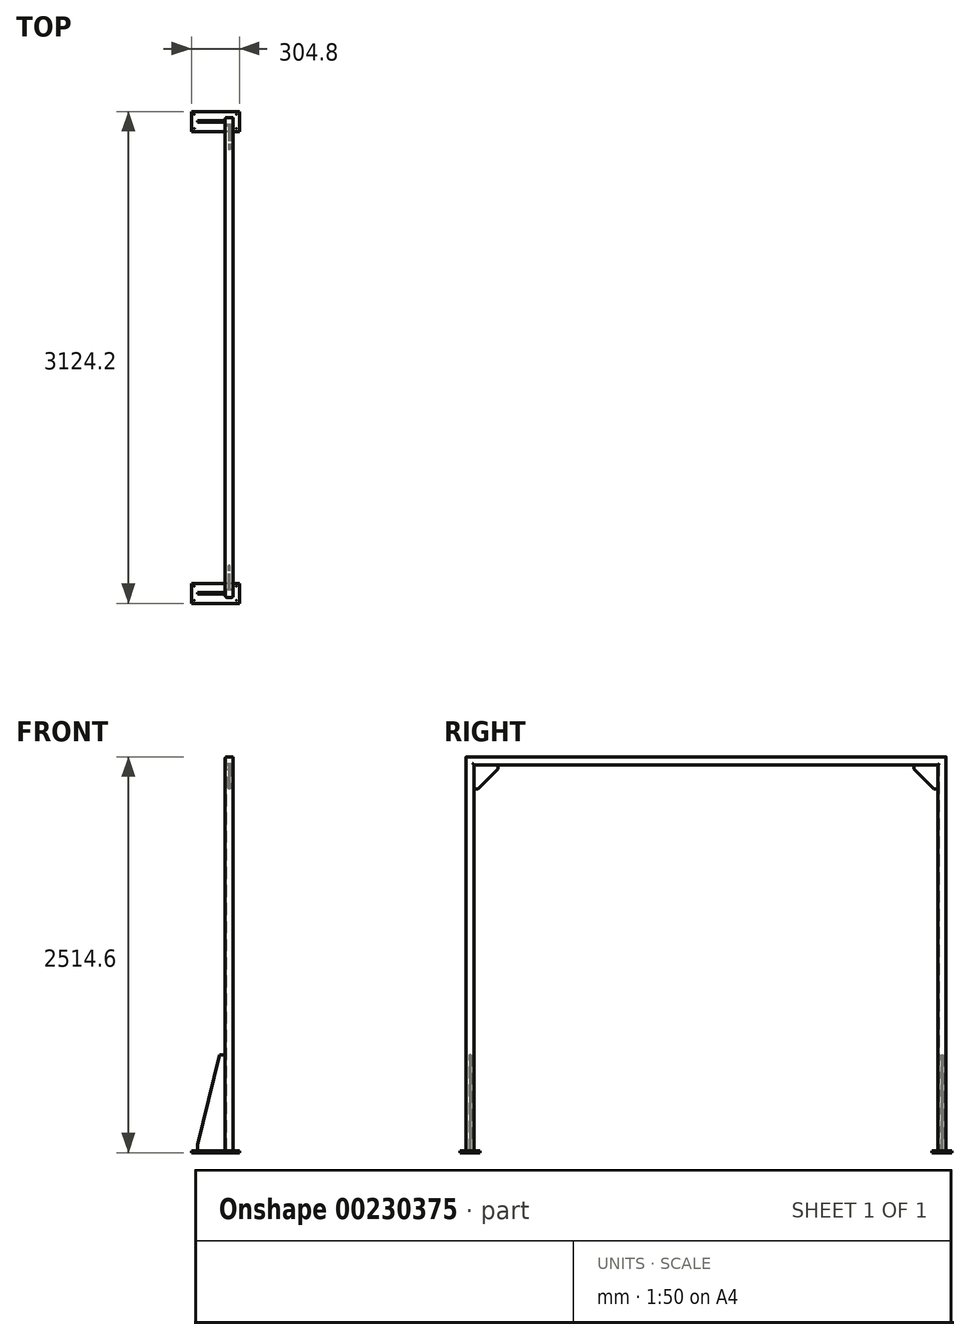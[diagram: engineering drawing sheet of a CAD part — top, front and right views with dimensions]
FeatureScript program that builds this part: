
annotation { "Feature Type Name" : "Feature", "Feature Type Description" : "" }
export const myFeature = defineFeature(function(context is Context, id is Id, definition is map)
    precondition{}
    {
        {
            var Q0;
            Q0=qCreatedBy(makeId("Right.planeOp"),FACE);
            var sketch = newSketch(context, id + "F0", { "sketchPlane" : qUnion([Q0])});
            skLineSegment(sketch, "E0.top", {"start": v(-1524, 2501.9) * mm, "end": v(1524, 2501.9) * mm});
            skLineSegment(sketch, "E0.left", {"start": v(-1524, 0) * mm, "end": v(-1524, 2501.9) * mm});
            skLineSegment(sketch, "E0.right", {"start": v(1524, 0) * mm, "end": v(1524, 2501.9) * mm});
            skSolve(sketch);
        }
        {
            var Q0;
            Q0=qCreatedBy(makeId("Top.planeOp"),FACE);
            var sketch = newSketch(context, id + "F1", { "sketchPlane" : qUnion([Q0])});
            skPoint(sketch, "E1.0", {"position": v(0, -1524) * mm});
            skLineSegment(sketch, "E2", {"start": v(0, -1524) * mm, "end": v(15.75, -1524) * mm});
            skLineSegment(sketch, "E3", {"start": v(25.4, -1514.35) * mm, "end": v(25.4, -1482.85) * mm});
            skLineSegment(sketch, "E4", {"start": v(15.75, -1473.2) * mm, "end": v(-15.75, -1473.2) * mm});
            skLineSegment(sketch, "E5", {"start": v(-25.4, -1482.85) * mm, "end": v(-25.4, -1514.35) * mm});
            skLineSegment(sketch, "E6", {"start": v(-15.75, -1524) * mm, "end": v(0, -1524) * mm});
            skPoint(sketch, "E7.visualSharp", {"position": v(25.4, -1524) * mm});
            skArc(sketch, "E7.filletArc", {"start": v(15.75, -1524) * mm, "mid": v(22.57, -1521.17) * mm, "end": v(25.4, -1514.35) * mm});
            skPoint(sketch, "E8.visualSharp", {"position": v(25.4, -1473.2) * mm});
            skArc(sketch, "E8.filletArc", {"start": v(25.4, -1482.85) * mm, "mid": v(22.57, -1476.03) * mm, "end": v(15.75, -1473.2) * mm});
            skPoint(sketch, "E9.visualSharp", {"position": v(-25.4, -1473.2) * mm});
            skArc(sketch, "E9.filletArc", {"start": v(-15.75, -1473.2) * mm, "mid": v(-22.57, -1476.03) * mm, "end": v(-25.4, -1482.85) * mm});
            skPoint(sketch, "E10.visualSharp", {"position": v(-25.4, -1524) * mm});
            skArc(sketch, "E10.filletArc", {"start": v(-25.4, -1514.35) * mm, "mid": v(-22.57, -1521.17) * mm, "end": v(-15.75, -1524) * mm});
            skLineSegment(sketch, "E11.0", {"start": v(-15.75, -1519.24) * mm, "end": v(0, -1519.24) * mm});
            skArc(sketch, "E11.1", {"start": v(-20.64, -1514.35) * mm, "mid": v(-19.2, -1517.8) * mm, "end": v(-15.75, -1519.24) * mm});
            skLineSegment(sketch, "E11.2", {"start": v(-20.64, -1482.85) * mm, "end": v(-20.64, -1514.35) * mm});
            skArc(sketch, "E11.3", {"start": v(-15.75, -1477.96) * mm, "mid": v(-19.2, -1479.4) * mm, "end": v(-20.64, -1482.85) * mm});
            skArc(sketch, "E11.4", {"start": v(15.75, -1519.24) * mm, "mid": v(19.2, -1517.8) * mm, "end": v(20.64, -1514.35) * mm});
            skLineSegment(sketch, "E11.5", {"start": v(20.64, -1514.35) * mm, "end": v(20.64, -1482.85) * mm});
            skArc(sketch, "E11.6", {"start": v(20.64, -1482.85) * mm, "mid": v(19.2, -1479.4) * mm, "end": v(15.75, -1477.96) * mm});
            skLineSegment(sketch, "E11.7", {"start": v(15.75, -1477.96) * mm, "end": v(-15.75, -1477.96) * mm});
            skLineSegment(sketch, "E12.0", {"start": v(0, -1519.24) * mm, "end": v(15.75, -1519.24) * mm});
            skSolve(sketch);
        }
        {
            var Q0;
            Q0=makeQuery(id+"F1.imprint","IMPRINT",FACE,{"disambiguationData":[TD([[makeQuery(id+"F1.imprint","IMPRINT",EDGE,{"derivedFrom":sQuery(id+"F1.wireOp",EDGE,"E2")}),1.0]])]});
            var Q1;
            Q1=sQuery(id+"F0.wireOp",EDGE,"E0.left");
            var Q2;
            Q2=sQuery(id+"F0.wireOp",EDGE,"E0.top");
            var Q3;
            Q3=sQuery(id+"F0.wireOp",EDGE,"E0.right");
            sweep(context, id + "F2", {"profiles" : qUnion([Q0]), "path" : qUnion([Q1, Q2, Q3])});
        }
        {
            var Q0;
            Q0=makeQuery(id+"F2.opSweep","CAP_FACE",FACE,{"disambiguationData":[OSD([sQuery(id+"F0.wireOp",VERTEX,"E0.left.start"),sQuery(id+"F1.wireOp",EDGE,"E2"),sQuery(id+"F1.wireOp",EDGE,"E3"),sQuery(id+"F1.wireOp",EDGE,"E4"),sQuery(id+"F1.wireOp",EDGE,"E5"),sQuery(id+"F1.wireOp",EDGE,"E6"),sQuery(id+"F1.wireOp",EDGE,"E7.filletArc"),sQuery(id+"F1.wireOp",EDGE,"E8.filletArc"),sQuery(id+"F1.wireOp",EDGE,"E9.filletArc"),sQuery(id+"F1.wireOp",EDGE,"E10.filletArc"),sQuery(id+"F1.wireOp",EDGE,"E11.0"),sQuery(id+"F1.wireOp",EDGE,"E11.1"),sQuery(id+"F1.wireOp",EDGE,"E11.2"),sQuery(id+"F1.wireOp",EDGE,"E11.3"),sQuery(id+"F1.wireOp",EDGE,"E11.4"),sQuery(id+"F1.wireOp",EDGE,"E11.5"),sQuery(id+"F1.wireOp",EDGE,"E11.6"),sQuery(id+"F1.wireOp",EDGE,"E11.7"),sQuery(id+"F1.wireOp",EDGE,"E12.0")])],"isStart":true});
            var sketch = newSketch(context, id + "F3", { "sketchPlane" : qUnion([Q0])});
            skLineSegment(sketch, "E13.0", {"start": v(-15.75, 1524) * mm, "end": v(15.75, 1524) * mm, "construction": true});
            skLineSegment(sketch, "E14.0", {"start": v(15.75, 1473.2) * mm, "end": v(-15.75, 1473.2) * mm, "construction": true});
            skLineSegment(sketch, "E15", {"start": v(0, 1524) * mm, "end": v(0, 1473.2) * mm, "construction": true});
            skLineSegment(sketch, "E16.bottom", {"start": v(63.5, 1562.1) * mm, "end": v(-63.5, 1562.1) * mm});
            skLineSegment(sketch, "E16.top", {"start": v(63.5, 1435.1) * mm, "end": v(-63.5, 1435.1) * mm});
            skLineSegment(sketch, "E16.left", {"start": v(63.5, 1562.1) * mm, "end": v(63.5, 1435.1) * mm});
            skLineSegment(sketch, "E16.right", {"start": v(-63.5, 1562.1) * mm, "end": v(-63.5, 1435.1) * mm});
            skPoint(sketch, "E16.middle", {"position": v(0, 1498.6) * mm});
            skLineSegment(sketch, "E17.bottom", {"start": v(-63.5, 1435.1) * mm, "end": v(-241.3, 1435.1) * mm});
            skLineSegment(sketch, "E17.top", {"start": v(-63.5, 1562.1) * mm, "end": v(-241.3, 1562.1) * mm});
            skLineSegment(sketch, "E17.left", {"start": v(-63.5, 1435.1) * mm, "end": v(-63.5, 1562.1) * mm});
            skLineSegment(sketch, "E17.right", {"start": v(-241.3, 1435.1) * mm, "end": v(-241.3, 1562.1) * mm});
            skLineSegment(sketch, "E18.0", {"start": v(-15.75, -1473.2) * mm, "end": v(15.75, -1473.2) * mm, "construction": true});
            skLineSegment(sketch, "E19.0", {"start": v(-15.75, -1524) * mm, "end": v(15.75, -1524) * mm, "construction": true});
            skLineSegment(sketch, "E20", {"start": v(0, -1473.2) * mm, "end": v(0, -1524) * mm, "construction": true});
            skLineSegment(sketch, "E21", {"start": v(0, -1501.83) * mm, "end": v(-72.48, -1501.83) * mm, "construction": true});
            skSolve(sketch);
        }
        {
            var Q0;
            Q0 = qSketchRegion(id + "F3", true);
            extrude(context, id + "F4", {"entities" : qUnion([Q0]), "depth" : 12.7 * mm});
        }
        {
            var Q0;
            Q0=makeQuery(id+"F4.opExtrude","SWEPT_FACE",FACE,{"disambiguationData":[OSD([sQuery(id+"F3.wireOp",EDGE,"E16.top"),sQuery(id+"F3.wireOp",EDGE,"E17.bottom")])]});
            var Q1;
            Q1=makeQuery(id+"F4.opExtrude","SWEPT_FACE",FACE,{"disambiguationData":[OSD([sQuery(id+"F3.wireOp",EDGE,"E16.bottom"),sQuery(id+"F3.wireOp",EDGE,"E17.top")])]});
            cPlane(context, id + "F5", {"entities" : qUnion([Q0, Q1]), "cplaneType" : CPlaneType.MID_PLANE, "offset" : 25.4 * mm, "width" : 152.4 * mm, "height" : 152.4 * mm});
        }
        {
            var Q0;
            Q0=qCreatedBy(id+"F5.planeOp",FACE);
            var sketch = newSketch(context, id + "F6", { "sketchPlane" : qUnion([Q0])});
            skLineSegment(sketch, "E22.0", {"start": v(25.4, 2492.25) * mm, "end": v(25.4, 0) * mm, "construction": true});
            skLineSegment(sketch, "E23.bottom", {"start": v(25.4, 0) * mm, "end": v(203.2, 0) * mm});
            skLineSegment(sketch, "E23.top", {"start": v(25.4, 609.6) * mm, "end": v(63.5, 609.6) * mm});
            skLineSegment(sketch, "E23.left", {"start": v(25.4, 0) * mm, "end": v(25.4, 609.6) * mm});
            skLineSegment(sketch, "E23.right", {"start": v(203.2, 0) * mm, "end": v(203.2, 38.1) * mm});
            skLineSegment(sketch, "E24.0", {"start": v(25.4, 38.1) * mm, "end": v(203.2, 38.1) * mm});
            skLineSegment(sketch, "E25.0", {"start": v(63.5, 2492.25) * mm, "end": v(63.5, 0) * mm});
            skLineSegment(sketch, "E26", {"start": v(63.5, 609.6) * mm, "end": v(203.2, 38.1) * mm});
            skSolve(sketch);
        }
        {
            var Q0;
            Q0 = qSketchRegion(id + "F6", true);
            extrude(context, id + "F7", {"entities" : qUnion([Q0]), "endBound" : BoundingType.SYMMETRIC, "depth" : 9.65 * mm});
        }
        {
            var Q0;
            Q0=makeQuery(id+"F4.opExtrude","CAP_FACE",FACE,{"disambiguationData":[OSD([sQuery(id+"F3.wireOp",EDGE,"E16.bottom"),sQuery(id+"F3.wireOp",EDGE,"E16.top"),sQuery(id+"F3.wireOp",EDGE,"E16.left"),sQuery(id+"F3.wireOp",EDGE,"E17.bottom"),sQuery(id+"F3.wireOp",EDGE,"E17.top"),sQuery(id+"F3.wireOp",EDGE,"E17.right")])],"isStart":false});
            var sketch = newSketch(context, id + "F8", { "sketchPlane" : qUnion([Q0])});
            skLineSegment(sketch, "E27.0", {"start": v(-222.25, 1435.1) * mm, "end": v(-222.25, 1562.1) * mm, "construction": true});
            skLineSegment(sketch, "E28.0", {"start": v(63.5, 1543.05) * mm, "end": v(-266.7, 1543.05) * mm, "construction": true});
            skLineSegment(sketch, "E29.0", {"start": v(44.45, 1562.1) * mm, "end": v(44.45, 1435.1) * mm, "construction": true});
            skLineSegment(sketch, "E30.0", {"start": v(63.5, 1454.15) * mm, "end": v(-266.7, 1454.15) * mm, "construction": true});
            skPoint(sketch, "E31", {"position": v(-222.25, 1454.15) * mm});
            skPoint(sketch, "E32", {"position": v(-222.25, 1543.05) * mm});
            skPoint(sketch, "E33", {"position": v(44.45, 1543.05) * mm});
            skPoint(sketch, "E34", {"position": v(44.45, 1454.15) * mm});
            skSolve(sketch);
        }
        {
            var Q0;
            Q0=sQuery(id+"F8.wireOp",VERTEX,"E31");
            var Q1;
            Q1=sQuery(id+"F8.wireOp",VERTEX,"E32");
            var Q2;
            Q2=sQuery(id+"F8.wireOp",VERTEX,"E33");
            var Q3;
            Q3=sQuery(id+"F8.wireOp",VERTEX,"E34");
            var Q4;
            Q4=makeQuery(id+"F4.opExtrude","SWEPT_BODY",BODY,{"disambiguationData":[OSD([sQuery(id+"F3.wireOp",EDGE,"E16.bottom"),sQuery(id+"F3.wireOp",EDGE,"E16.top"),sQuery(id+"F3.wireOp",EDGE,"E16.left"),sQuery(id+"F3.wireOp",EDGE,"E17.bottom"),sQuery(id+"F3.wireOp",EDGE,"E17.top"),sQuery(id+"F3.wireOp",EDGE,"E17.right")])]});
            hole(context, id + "F9", {"style" : HoleStyle.SIMPLE, "endStyle" : HoleEndStyle.THROUGH, "standardTappedOrClearance" : lookupTablePath({ "standard" : "ANSI", "size" : "9/16 (0.56)", "type" : "Drilled" }), "standardBlindInLast" : lookupTablePath({ "standard" : "ANSI", "size" : "9/16", "type" : "Drilled" }), "holeDiameter" : 9 / 406.4 * mm, "startFromSketch" : true, "locations" : qUnion([Q0, Q1, Q2, Q3]), "scope" : qUnion([Q4]), "isTappedThrough" : true});
        }
        {
            var Q0;
            Q0=makeQuery(id+"F4.opExtrude","SWEPT_BODY",BODY,{"disambiguationData":[OSD([sQuery(id+"F3.wireOp",EDGE,"E16.bottom"),sQuery(id+"F3.wireOp",EDGE,"E16.top"),sQuery(id+"F3.wireOp",EDGE,"E16.left"),sQuery(id+"F3.wireOp",EDGE,"E17.bottom"),sQuery(id+"F3.wireOp",EDGE,"E17.top"),sQuery(id+"F3.wireOp",EDGE,"E17.right")])]});
            var Q1;
            Q1=makeQuery(id+"F7.opExtrude","SWEPT_BODY",BODY,{"disambiguationData":[OSD([sQuery(id+"F6.wireOp",EDGE,"E23.bottom"),sQuery(id+"F6.wireOp",EDGE,"E23.top"),sQuery(id+"F6.wireOp",EDGE,"E23.left"),sQuery(id+"F6.wireOp",EDGE,"E23.right"),sQuery(id+"F6.wireOp",EDGE,"E26")])]});
            var Q2;
            Q2=qCreatedBy(makeId("Front.planeOp"),FACE);
            mirror(context, id + "F10", {"entities" : qUnion([Q0, Q1]), "mirrorPlane" : qUnion([Q2])});
        }
        {
            var Q0;
            Q0=makeQuery(id+"F2.opSweep","SWEPT_FACE",FACE,{"disambiguationData":[OSD([sQuery(id+"F0.wireOp",EDGE,"E0.left"),sQuery(id+"F1.wireOp",EDGE,"E3")])]});
            var Q1;
            Q1=makeQuery(id+"F2.opSweep","SWEPT_FACE",FACE,{"disambiguationData":[OSD([sQuery(id+"F0.wireOp",EDGE,"E0.left"),sQuery(id+"F1.wireOp",EDGE,"E5")])]});
            cPlane(context, id + "F11", {"entities" : qUnion([Q0, Q1]), "cplaneType" : CPlaneType.MID_PLANE, "offset" : 25.4 * mm, "width" : 152.4 * mm, "height" : 152.4 * mm});
        }
        {
            var Q0;
            Q0=qCreatedBy(id+"F11.planeOp",FACE);
            var sketch = newSketch(context, id + "F12", { "sketchPlane" : qUnion([Q0])});
            skLineSegment(sketch, "E35.0", {"start": v(-1473.2, 2451.1) * mm, "end": v(1473.2, 2451.1) * mm, "construction": true});
            skLineSegment(sketch, "E36.0", {"start": v(-1473.2, 0) * mm, "end": v(-1473.2, 2451.1) * mm, "construction": true});
            skLineSegment(sketch, "E37.bottom", {"start": v(-1473.2, 2451.1) * mm, "end": v(-1320.8, 2451.1) * mm});
            skLineSegment(sketch, "E37.top", {"start": v(-1473.2, 2298.7) * mm, "end": v(-1447.8, 2298.7) * mm});
            skLineSegment(sketch, "E37.left", {"start": v(-1473.2, 2451.1) * mm, "end": v(-1473.2, 2298.7) * mm});
            skLineSegment(sketch, "E37.right", {"start": v(-1320.8, 2451.1) * mm, "end": v(-1320.8, 2425.7) * mm});
            skLineSegment(sketch, "E38.0", {"start": v(-1473.2, 2425.7) * mm, "end": v(1473.2, 2425.7) * mm, "construction": true});
            skLineSegment(sketch, "E39.0", {"start": v(-1447.8, 0) * mm, "end": v(-1447.8, 2451.1) * mm, "construction": true});
            skLineSegment(sketch, "E40", {"start": v(-1447.8, 2298.7) * mm, "end": v(-1320.8, 2425.7) * mm});
            skSolve(sketch);
        }
        {
            var Q0;
            Q0 = qSketchRegion(id + "F12", true);
            extrude(context, id + "F13", {"entities" : qUnion([Q0]), "endBound" : BoundingType.SYMMETRIC, "depth" : 9.52 * mm});
        }
        {
            var Q0;
            Q0=makeQuery(id+"F13.opExtrude","SWEPT_BODY",BODY,{"disambiguationData":[OSD([sQuery(id+"F12.wireOp",EDGE,"E37.bottom"),sQuery(id+"F12.wireOp",EDGE,"E37.top"),sQuery(id+"F12.wireOp",EDGE,"E37.left"),sQuery(id+"F12.wireOp",EDGE,"E37.right"),sQuery(id+"F12.wireOp",EDGE,"E40")])]});
            var Q1;
            Q1=qCreatedBy(makeId("Front.planeOp"),FACE);
            mirror(context, id + "F14", {"operationType" : NewBodyOperationType.ADD, "entities" : qUnion([Q0]), "mirrorPlane" : qUnion([Q1])});
        }
    });
